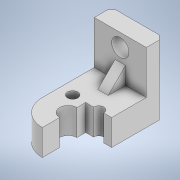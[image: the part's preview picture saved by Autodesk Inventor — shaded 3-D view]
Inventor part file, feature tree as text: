
AUTODESK INVENTOR PART (.ipt)
format: ipt  version: 2022 (Build 260153000, 153)  size: 159,744 bytes
history: native  units: mm
features: extrude x5, sketch x5, other x2
ambient origin geometry x8: Origin, YZ Plane, XZ Plane, XY Plane, X Axis, Y Axis, Z Axis, Center Point
bodies: Body1 (feature_tree)
feature tree (12):
  other  "Твердое тело1"
  extrude  "Выдавливание1"  Depth=80.0mm
  extrude  "Выдавливание2"  Depth=20.0mm
  extrude  "Выдавливание3"  Depth=12.0mm
  other  "РабПлоскость1"
  extrude  "Выдавливание4"  Depth=12.0mm
  extrude  "Выдавливание5"  Depth=30.0mm TaperAngle=0.0deg
  sketch  "Эскиз1"
  sketch  "Эскиз2"
  sketch  "Эскиз3"
  sketch  "Эскиз6"
  sketch  "Эскиз7"
